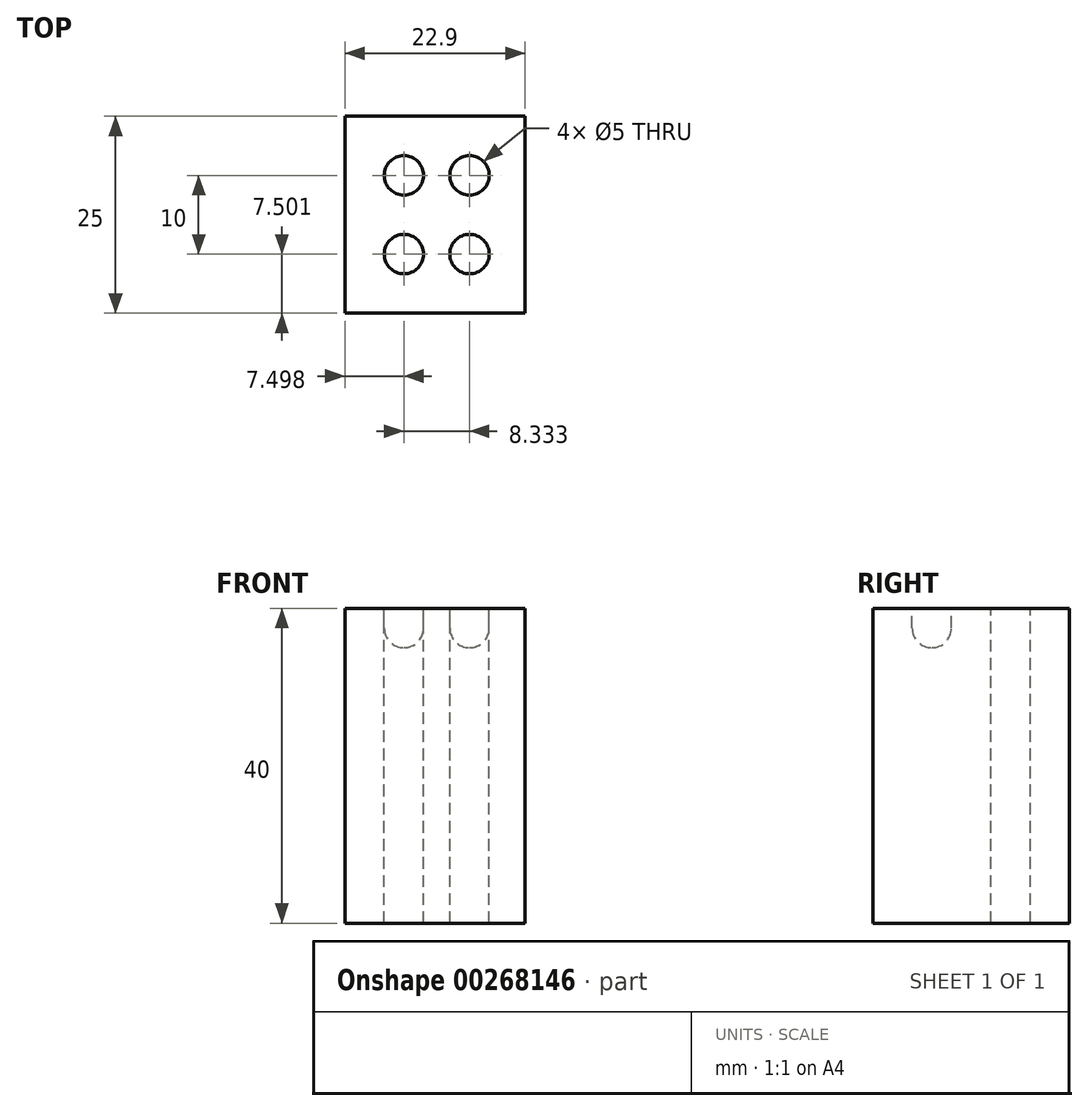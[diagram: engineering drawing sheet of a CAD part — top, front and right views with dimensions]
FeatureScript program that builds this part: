
annotation { "Feature Type Name" : "Feature", "Feature Type Description" : "" }
export const myFeature = defineFeature(function(context is Context, id is Id, definition is map)
    precondition{}
    {
        {
            var Q0;
            Q0=qCreatedBy(makeId("Top.planeOp"),FACE);
            var sketch = newSketch(context, id + "F0", { "sketchPlane" : qUnion([Q0])});
            skLineSegment(sketch, "E0.bottom", {"start": v(-42.9, 15.92) * mm, "end": v(-20, 15.92) * mm});
            skLineSegment(sketch, "E0.top", {"start": v(-42.9, -9.08) * mm, "end": v(-20, -9.08) * mm});
            skLineSegment(sketch, "E0.left", {"start": v(-42.9, 15.92) * mm, "end": v(-42.9, -9.08) * mm});
            skLineSegment(sketch, "E0.right", {"start": v(-20, 15.92) * mm, "end": v(-20, -9.08) * mm});
            skCircle(sketch, "E1", {"center": v(-35.4, 8.42) * mm, "radius": 2.5 * mm});
            skCircle(sketch, "E2.1.0.0", {"center": v(-27.06, 8.42) * mm, "radius": 2.5 * mm});
            skLineSegment(sketch, "E2.direction1", {"start": v(-35.4, 8.42) * mm, "end": v(-27.06, 8.42) * mm, "construction": true});
            skCircle(sketch, "E3", {"center": v(-35.4, -1.58) * mm, "radius": 2.5 * mm});
            skCircle(sketch, "E4.1.0.0", {"center": v(-27.06, -1.58) * mm, "radius": 2.5 * mm});
            skLineSegment(sketch, "E4.direction1", {"start": v(-35.4, -1.58) * mm, "end": v(-27.06, -1.58) * mm, "construction": true});
            skSolve(sketch);
        }
        {
            var Q0;
            Q0=makeQuery(id+"F0.imprint","IMPRINT",FACE,{"disambiguationData":[TD([[makeQuery(id+"F0.imprint","IMPRINT",EDGE,{"derivedFrom":sQuery(id+"F0.wireOp",EDGE,"E0.bottom")}),-1.0]])]});
            var Q1;
            Q1=makeQuery(id+"F0.imprint","IMPRINT",FACE,{"disambiguationData":[TD([[makeQuery(id+"F0.imprint","IMPRINT",EDGE,{"derivedFrom":sQuery(id+"F0.wireOp",EDGE,"E1")}),1.0]])]});
            var Q2;
            Q2=makeQuery(id+"F0.imprint","IMPRINT",FACE,{"disambiguationData":[TD([[makeQuery(id+"F0.imprint","IMPRINT",EDGE,{"derivedFrom":sQuery(id+"F0.wireOp",EDGE,"E2.1.0.0")}),1.0]])]});
            var Q3;
            Q3=makeQuery(id+"F0.imprint","IMPRINT",FACE,{"disambiguationData":[TD([[makeQuery(id+"F0.imprint","IMPRINT",EDGE,{"derivedFrom":sQuery(id+"F0.wireOp",EDGE,"E2.2.0.0")}),1.0]])]});
            var Q4;
            Q4=makeQuery(id+"F0.imprint","IMPRINT",FACE,{"disambiguationData":[TD([[makeQuery(id+"F0.imprint","IMPRINT",EDGE,{"derivedFrom":sQuery(id+"F0.wireOp",EDGE,"E2.3.0.0")}),1.0]])]});
            var Q5;
            Q5=makeQuery(id+"F0.imprint","IMPRINT",FACE,{"disambiguationData":[TD([[makeQuery(id+"F0.imprint","IMPRINT",EDGE,{"derivedFrom":sQuery(id+"F0.wireOp",EDGE,"E2.4.0.0")}),1.0]])]});
            var Q6;
            Q6=makeQuery(id+"F0.imprint","IMPRINT",FACE,{"disambiguationData":[TD([[makeQuery(id+"F0.imprint","IMPRINT",EDGE,{"derivedFrom":sQuery(id+"F0.wireOp",EDGE,"E2.5.0.0")}),1.0]])]});
            var Q7;
            Q7=makeQuery(id+"F0.imprint","IMPRINT",FACE,{"disambiguationData":[TD([[makeQuery(id+"F0.imprint","IMPRINT",EDGE,{"derivedFrom":sQuery(id+"F0.wireOp",EDGE,"E2.6.0.0")}),1.0]])]});
            var Q8;
            Q8=makeQuery(id+"F0.imprint","IMPRINT",FACE,{"disambiguationData":[TD([[makeQuery(id+"F0.imprint","IMPRINT",EDGE,{"derivedFrom":sQuery(id+"F0.wireOp",EDGE,"E2.7.0.0")}),1.0]])]});
            var Q9;
            Q9=makeQuery(id+"F0.imprint","IMPRINT",FACE,{"disambiguationData":[TD([[makeQuery(id+"F0.imprint","IMPRINT",EDGE,{"derivedFrom":sQuery(id+"F0.wireOp",EDGE,"E2.8.0.0")}),1.0]])]});
            var Q10;
            Q10=makeQuery(id+"F0.imprint","IMPRINT",FACE,{"disambiguationData":[TD([[makeQuery(id+"F0.imprint","IMPRINT",EDGE,{"derivedFrom":sQuery(id+"F0.wireOp",EDGE,"E2.9.0.0")}),1.0]])]});
            var Q11;
            Q11=makeQuery(id+"F0.imprint","IMPRINT",FACE,{"disambiguationData":[TD([[makeQuery(id+"F0.imprint","IMPRINT",EDGE,{"derivedFrom":sQuery(id+"F0.wireOp",EDGE,"E2.10.0.0")}),1.0]])]});
            var Q12;
            Q12=makeQuery(id+"F0.imprint","IMPRINT",FACE,{"disambiguationData":[TD([[makeQuery(id+"F0.imprint","IMPRINT",EDGE,{"derivedFrom":sQuery(id+"F0.wireOp",EDGE,"E2.11.0.0")}),1.0]])]});
            var Q13;
            Q13=makeQuery(id+"F0.imprint","IMPRINT",FACE,{"disambiguationData":[TD([[makeQuery(id+"F0.imprint","IMPRINT",EDGE,{"derivedFrom":sQuery(id+"F0.wireOp",EDGE,"E2.12.0.0")}),1.0]])]});
            var Q14;
            Q14=makeQuery(id+"F0.imprint","IMPRINT",FACE,{"disambiguationData":[TD([[makeQuery(id+"F0.imprint","IMPRINT",EDGE,{"derivedFrom":sQuery(id+"F0.wireOp",EDGE,"E2.13.0.0")}),1.0]])]});
            var Q15;
            Q15=makeQuery(id+"F0.imprint","IMPRINT",FACE,{"disambiguationData":[TD([[makeQuery(id+"F0.imprint","IMPRINT",EDGE,{"derivedFrom":sQuery(id+"F0.wireOp",EDGE,"E2.14.0.0")}),1.0]])]});
            var Q16;
            Q16=makeQuery(id+"F0.imprint","IMPRINT",FACE,{"disambiguationData":[TD([[makeQuery(id+"F0.imprint","IMPRINT",EDGE,{"derivedFrom":sQuery(id+"F0.wireOp",EDGE,"E4.14.0.0")}),1.0]])]});
            var Q17;
            Q17=makeQuery(id+"F0.imprint","IMPRINT",FACE,{"disambiguationData":[TD([[makeQuery(id+"F0.imprint","IMPRINT",EDGE,{"derivedFrom":sQuery(id+"F0.wireOp",EDGE,"E4.13.0.0")}),1.0]])]});
            var Q18;
            Q18=makeQuery(id+"F0.imprint","IMPRINT",FACE,{"disambiguationData":[TD([[makeQuery(id+"F0.imprint","IMPRINT",EDGE,{"derivedFrom":sQuery(id+"F0.wireOp",EDGE,"E4.12.0.0")}),1.0]])]});
            var Q19;
            Q19=makeQuery(id+"F0.imprint","IMPRINT",FACE,{"disambiguationData":[TD([[makeQuery(id+"F0.imprint","IMPRINT",EDGE,{"derivedFrom":sQuery(id+"F0.wireOp",EDGE,"E4.11.0.0")}),1.0]])]});
            var Q20;
            Q20=makeQuery(id+"F0.imprint","IMPRINT",FACE,{"disambiguationData":[TD([[makeQuery(id+"F0.imprint","IMPRINT",EDGE,{"derivedFrom":sQuery(id+"F0.wireOp",EDGE,"E4.10.0.0")}),1.0]])]});
            var Q21;
            Q21=makeQuery(id+"F0.imprint","IMPRINT",FACE,{"disambiguationData":[TD([[makeQuery(id+"F0.imprint","IMPRINT",EDGE,{"derivedFrom":sQuery(id+"F0.wireOp",EDGE,"E4.9.0.0")}),1.0]])]});
            var Q22;
            Q22=makeQuery(id+"F0.imprint","IMPRINT",FACE,{"disambiguationData":[TD([[makeQuery(id+"F0.imprint","IMPRINT",EDGE,{"derivedFrom":sQuery(id+"F0.wireOp",EDGE,"E4.8.0.0")}),1.0]])]});
            var Q23;
            Q23=makeQuery(id+"F0.imprint","IMPRINT",FACE,{"disambiguationData":[TD([[makeQuery(id+"F0.imprint","IMPRINT",EDGE,{"derivedFrom":sQuery(id+"F0.wireOp",EDGE,"E4.7.0.0")}),1.0]])]});
            var Q24;
            Q24=makeQuery(id+"F0.imprint","IMPRINT",FACE,{"disambiguationData":[TD([[makeQuery(id+"F0.imprint","IMPRINT",EDGE,{"derivedFrom":sQuery(id+"F0.wireOp",EDGE,"E4.6.0.0")}),1.0]])]});
            var Q25;
            Q25=makeQuery(id+"F0.imprint","IMPRINT",FACE,{"disambiguationData":[TD([[makeQuery(id+"F0.imprint","IMPRINT",EDGE,{"derivedFrom":sQuery(id+"F0.wireOp",EDGE,"E4.5.0.0")}),1.0]])]});
            var Q26;
            Q26=makeQuery(id+"F0.imprint","IMPRINT",FACE,{"disambiguationData":[TD([[makeQuery(id+"F0.imprint","IMPRINT",EDGE,{"derivedFrom":sQuery(id+"F0.wireOp",EDGE,"E4.4.0.0")}),1.0]])]});
            var Q27;
            Q27=makeQuery(id+"F0.imprint","IMPRINT",FACE,{"disambiguationData":[TD([[makeQuery(id+"F0.imprint","IMPRINT",EDGE,{"derivedFrom":sQuery(id+"F0.wireOp",EDGE,"E4.3.0.0")}),1.0]])]});
            var Q28;
            Q28=makeQuery(id+"F0.imprint","IMPRINT",FACE,{"disambiguationData":[TD([[makeQuery(id+"F0.imprint","IMPRINT",EDGE,{"derivedFrom":sQuery(id+"F0.wireOp",EDGE,"E4.2.0.0")}),1.0]])]});
            var Q29;
            Q29=makeQuery(id+"F0.imprint","IMPRINT",FACE,{"disambiguationData":[TD([[makeQuery(id+"F0.imprint","IMPRINT",EDGE,{"derivedFrom":sQuery(id+"F0.wireOp",EDGE,"E4.1.0.0")}),1.0]])]});
            var Q30;
            Q30=makeQuery(id+"F0.imprint","IMPRINT",FACE,{"disambiguationData":[TD([[makeQuery(id+"F0.imprint","IMPRINT",EDGE,{"derivedFrom":sQuery(id+"F0.wireOp",EDGE,"E3")}),1.0]])]});
            extrude(context, id + "F1", {"entities" : qUnion([Q0, Q1, Q2, Q3, Q4, Q5, Q6, Q7, Q8, Q9, Q10, Q11, Q12, Q13, Q14, Q15, Q16, Q17, Q18, Q19, Q20, Q21, Q22, Q23, Q24, Q25, Q26, Q27, Q28, Q29, Q30]), "oppositeDirection" : true, "depth" : 40 * mm});
        }
        {
            var Q0;
            Q0=makeQuery(id+"F0.imprint","IMPRINT",FACE,{"disambiguationData":[TD([[makeQuery(id+"F0.imprint","IMPRINT",EDGE,{"derivedFrom":sQuery(id+"F0.wireOp",EDGE,"E1")}),1.0]])]});
            var Q1;
            Q1=makeQuery(id+"F0.imprint","IMPRINT",FACE,{"disambiguationData":[TD([[makeQuery(id+"F0.imprint","IMPRINT",EDGE,{"derivedFrom":sQuery(id+"F0.wireOp",EDGE,"E2.1.0.0")}),1.0]])]});
            var Q2;
            Q2=makeQuery(id+"F0.imprint","IMPRINT",FACE,{"disambiguationData":[TD([[makeQuery(id+"F0.imprint","IMPRINT",EDGE,{"derivedFrom":sQuery(id+"F0.wireOp",EDGE,"E2.2.0.0")}),1.0]])]});
            var Q3;
            Q3=makeQuery(id+"F0.imprint","IMPRINT",FACE,{"disambiguationData":[TD([[makeQuery(id+"F0.imprint","IMPRINT",EDGE,{"derivedFrom":sQuery(id+"F0.wireOp",EDGE,"E2.3.0.0")}),1.0]])]});
            var Q4;
            Q4=makeQuery(id+"F0.imprint","IMPRINT",FACE,{"disambiguationData":[TD([[makeQuery(id+"F0.imprint","IMPRINT",EDGE,{"derivedFrom":sQuery(id+"F0.wireOp",EDGE,"E2.4.0.0")}),1.0]])]});
            var Q5;
            Q5=makeQuery(id+"F0.imprint","IMPRINT",FACE,{"disambiguationData":[TD([[makeQuery(id+"F0.imprint","IMPRINT",EDGE,{"derivedFrom":sQuery(id+"F0.wireOp",EDGE,"E2.5.0.0")}),1.0]])]});
            var Q6;
            Q6=makeQuery(id+"F0.imprint","IMPRINT",FACE,{"disambiguationData":[TD([[makeQuery(id+"F0.imprint","IMPRINT",EDGE,{"derivedFrom":sQuery(id+"F0.wireOp",EDGE,"E2.6.0.0")}),1.0]])]});
            var Q7;
            Q7=makeQuery(id+"F0.imprint","IMPRINT",FACE,{"disambiguationData":[TD([[makeQuery(id+"F0.imprint","IMPRINT",EDGE,{"derivedFrom":sQuery(id+"F0.wireOp",EDGE,"E2.7.0.0")}),1.0]])]});
            var Q8;
            Q8=makeQuery(id+"F0.imprint","IMPRINT",FACE,{"disambiguationData":[TD([[makeQuery(id+"F0.imprint","IMPRINT",EDGE,{"derivedFrom":sQuery(id+"F0.wireOp",EDGE,"E2.8.0.0")}),1.0]])]});
            var Q9;
            Q9=makeQuery(id+"F0.imprint","IMPRINT",FACE,{"disambiguationData":[TD([[makeQuery(id+"F0.imprint","IMPRINT",EDGE,{"derivedFrom":sQuery(id+"F0.wireOp",EDGE,"E2.9.0.0")}),1.0]])]});
            var Q10;
            Q10=makeQuery(id+"F0.imprint","IMPRINT",FACE,{"disambiguationData":[TD([[makeQuery(id+"F0.imprint","IMPRINT",EDGE,{"derivedFrom":sQuery(id+"F0.wireOp",EDGE,"E2.10.0.0")}),1.0]])]});
            var Q11;
            Q11=makeQuery(id+"F0.imprint","IMPRINT",FACE,{"disambiguationData":[TD([[makeQuery(id+"F0.imprint","IMPRINT",EDGE,{"derivedFrom":sQuery(id+"F0.wireOp",EDGE,"E2.11.0.0")}),1.0]])]});
            var Q12;
            Q12=makeQuery(id+"F0.imprint","IMPRINT",FACE,{"disambiguationData":[TD([[makeQuery(id+"F0.imprint","IMPRINT",EDGE,{"derivedFrom":sQuery(id+"F0.wireOp",EDGE,"E2.12.0.0")}),1.0]])]});
            var Q13;
            Q13=makeQuery(id+"F0.imprint","IMPRINT",FACE,{"disambiguationData":[TD([[makeQuery(id+"F0.imprint","IMPRINT",EDGE,{"derivedFrom":sQuery(id+"F0.wireOp",EDGE,"E2.13.0.0")}),1.0]])]});
            var Q14;
            Q14=makeQuery(id+"F0.imprint","IMPRINT",FACE,{"disambiguationData":[TD([[makeQuery(id+"F0.imprint","IMPRINT",EDGE,{"derivedFrom":sQuery(id+"F0.wireOp",EDGE,"E2.14.0.0")}),1.0]])]});
            extrude(context, id + "F2", {"entities" : qUnion([Q0, Q1, Q2, Q3, Q4, Q5, Q6, Q7, Q8, Q9, Q10, Q11, Q12, Q13, Q14]), "operationType" : NewBodyOperationType.REMOVE, "oppositeDirection" : true, "depth" : 40 * mm});
        }
        {
            var Q0;
            Q0=makeQuery(id+"F0.imprint","IMPRINT",FACE,{"disambiguationData":[TD([[makeQuery(id+"F0.imprint","IMPRINT",EDGE,{"derivedFrom":sQuery(id+"F0.wireOp",EDGE,"E3")}),1.0]])]});
            var Q1;
            Q1=makeQuery(id+"F0.imprint","IMPRINT",FACE,{"disambiguationData":[TD([[makeQuery(id+"F0.imprint","IMPRINT",EDGE,{"derivedFrom":sQuery(id+"F0.wireOp",EDGE,"E4.1.0.0")}),1.0]])]});
            var Q2;
            Q2=makeQuery(id+"F0.imprint","IMPRINT",FACE,{"disambiguationData":[TD([[makeQuery(id+"F0.imprint","IMPRINT",EDGE,{"derivedFrom":sQuery(id+"F0.wireOp",EDGE,"E4.2.0.0")}),1.0]])]});
            var Q3;
            Q3=makeQuery(id+"F0.imprint","IMPRINT",FACE,{"disambiguationData":[TD([[makeQuery(id+"F0.imprint","IMPRINT",EDGE,{"derivedFrom":sQuery(id+"F0.wireOp",EDGE,"E4.3.0.0")}),1.0]])]});
            var Q4;
            Q4=makeQuery(id+"F0.imprint","IMPRINT",FACE,{"disambiguationData":[TD([[makeQuery(id+"F0.imprint","IMPRINT",EDGE,{"derivedFrom":sQuery(id+"F0.wireOp",EDGE,"E4.4.0.0")}),1.0]])]});
            var Q5;
            Q5=makeQuery(id+"F0.imprint","IMPRINT",FACE,{"disambiguationData":[TD([[makeQuery(id+"F0.imprint","IMPRINT",EDGE,{"derivedFrom":sQuery(id+"F0.wireOp",EDGE,"E4.5.0.0")}),1.0]])]});
            var Q6;
            Q6=makeQuery(id+"F0.imprint","IMPRINT",FACE,{"disambiguationData":[TD([[makeQuery(id+"F0.imprint","IMPRINT",EDGE,{"derivedFrom":sQuery(id+"F0.wireOp",EDGE,"E4.6.0.0")}),1.0]])]});
            var Q7;
            Q7=makeQuery(id+"F0.imprint","IMPRINT",FACE,{"disambiguationData":[TD([[makeQuery(id+"F0.imprint","IMPRINT",EDGE,{"derivedFrom":sQuery(id+"F0.wireOp",EDGE,"E4.7.0.0")}),1.0]])]});
            var Q8;
            Q8=makeQuery(id+"F0.imprint","IMPRINT",FACE,{"disambiguationData":[TD([[makeQuery(id+"F0.imprint","IMPRINT",EDGE,{"derivedFrom":sQuery(id+"F0.wireOp",EDGE,"E4.8.0.0")}),1.0]])]});
            var Q9;
            Q9=makeQuery(id+"F0.imprint","IMPRINT",FACE,{"disambiguationData":[TD([[makeQuery(id+"F0.imprint","IMPRINT",EDGE,{"derivedFrom":sQuery(id+"F0.wireOp",EDGE,"E4.9.0.0")}),1.0]])]});
            var Q10;
            Q10=makeQuery(id+"F0.imprint","IMPRINT",FACE,{"disambiguationData":[TD([[makeQuery(id+"F0.imprint","IMPRINT",EDGE,{"derivedFrom":sQuery(id+"F0.wireOp",EDGE,"E4.10.0.0")}),1.0]])]});
            var Q11;
            Q11=makeQuery(id+"F0.imprint","IMPRINT",FACE,{"disambiguationData":[TD([[makeQuery(id+"F0.imprint","IMPRINT",EDGE,{"derivedFrom":sQuery(id+"F0.wireOp",EDGE,"E4.11.0.0")}),1.0]])]});
            var Q12;
            Q12=makeQuery(id+"F0.imprint","IMPRINT",FACE,{"disambiguationData":[TD([[makeQuery(id+"F0.imprint","IMPRINT",EDGE,{"derivedFrom":sQuery(id+"F0.wireOp",EDGE,"E4.12.0.0")}),1.0]])]});
            var Q13;
            Q13=makeQuery(id+"F0.imprint","IMPRINT",FACE,{"disambiguationData":[TD([[makeQuery(id+"F0.imprint","IMPRINT",EDGE,{"derivedFrom":sQuery(id+"F0.wireOp",EDGE,"E4.13.0.0")}),1.0]])]});
            var Q14;
            Q14=makeQuery(id+"F0.imprint","IMPRINT",FACE,{"disambiguationData":[TD([[makeQuery(id+"F0.imprint","IMPRINT",EDGE,{"derivedFrom":sQuery(id+"F0.wireOp",EDGE,"E4.14.0.0")}),1.0]])]});
            extrude(context, id + "F3", {"entities" : qUnion([Q0, Q1, Q2, Q3, Q4, Q5, Q6, Q7, Q8, Q9, Q10, Q11, Q12, Q13, Q14]), "operationType" : NewBodyOperationType.REMOVE, "oppositeDirection" : true, "depth" : 5 * mm});
        }
        {
            var Q0;
            Q0=makeQuery(id+"F3.boolean.opBoolean","COPY",EDGE,{"derivedFrom":makeQuery(id+"F3.opExtrude","CAP_EDGE",EDGE,{"disambiguationData":[OSD([sQuery(id+"F0.wireOp",EDGE,"E3")])],"isStart":false})});
            var Q1;
            Q1=makeQuery(id+"F3.boolean.opBoolean","COPY",EDGE,{"derivedFrom":makeQuery(id+"F3.opExtrude","CAP_EDGE",EDGE,{"disambiguationData":[OSD([sQuery(id+"F0.wireOp",EDGE,"E4.1.0.0")])],"isStart":false})});
            var Q2;
            Q2=makeQuery(id+"F3.boolean.opBoolean","COPY",EDGE,{"derivedFrom":makeQuery(id+"F3.opExtrude","CAP_EDGE",EDGE,{"disambiguationData":[OSD([sQuery(id+"F0.wireOp",EDGE,"E4.2.0.0")])],"isStart":false})});
            var Q3;
            Q3=makeQuery(id+"F3.boolean.opBoolean","COPY",EDGE,{"derivedFrom":makeQuery(id+"F3.opExtrude","CAP_EDGE",EDGE,{"disambiguationData":[OSD([sQuery(id+"F0.wireOp",EDGE,"E4.3.0.0")])],"isStart":false})});
            var Q4;
            Q4=makeQuery(id+"F3.boolean.opBoolean","COPY",EDGE,{"derivedFrom":makeQuery(id+"F3.opExtrude","CAP_EDGE",EDGE,{"disambiguationData":[OSD([sQuery(id+"F0.wireOp",EDGE,"E4.4.0.0")])],"isStart":false})});
            var Q5;
            Q5=makeQuery(id+"F3.boolean.opBoolean","COPY",EDGE,{"derivedFrom":makeQuery(id+"F3.opExtrude","CAP_EDGE",EDGE,{"disambiguationData":[OSD([sQuery(id+"F0.wireOp",EDGE,"E4.5.0.0")])],"isStart":false})});
            var Q6;
            Q6=makeQuery(id+"F3.boolean.opBoolean","COPY",EDGE,{"derivedFrom":makeQuery(id+"F3.opExtrude","CAP_EDGE",EDGE,{"disambiguationData":[OSD([sQuery(id+"F0.wireOp",EDGE,"E4.6.0.0")])],"isStart":false})});
            var Q7;
            Q7=makeQuery(id+"F3.boolean.opBoolean","COPY",EDGE,{"derivedFrom":makeQuery(id+"F3.opExtrude","CAP_EDGE",EDGE,{"disambiguationData":[OSD([sQuery(id+"F0.wireOp",EDGE,"E4.7.0.0")])],"isStart":false})});
            var Q8;
            Q8=makeQuery(id+"F3.boolean.opBoolean","COPY",FACE,{"derivedFrom":makeQuery(id+"F3.opExtrude","CAP_FACE",FACE,{"disambiguationData":[OSD([sQuery(id+"F0.wireOp",EDGE,"E4.8.0.0")])],"isStart":false})});
            var Q9;
            Q9=makeQuery(id+"F3.boolean.opBoolean","COPY",EDGE,{"derivedFrom":makeQuery(id+"F3.opExtrude","CAP_EDGE",EDGE,{"disambiguationData":[OSD([sQuery(id+"F0.wireOp",EDGE,"E4.9.0.0")])],"isStart":false})});
            var Q10;
            Q10=makeQuery(id+"F3.boolean.opBoolean","COPY",EDGE,{"derivedFrom":makeQuery(id+"F3.opExtrude","CAP_EDGE",EDGE,{"disambiguationData":[OSD([sQuery(id+"F0.wireOp",EDGE,"E4.10.0.0")])],"isStart":false})});
            var Q11;
            Q11=makeQuery(id+"F3.boolean.opBoolean","COPY",FACE,{"derivedFrom":makeQuery(id+"F3.opExtrude","CAP_FACE",FACE,{"disambiguationData":[OSD([sQuery(id+"F0.wireOp",EDGE,"E4.11.0.0")])],"isStart":false})});
            var Q12;
            Q12=makeQuery(id+"F3.boolean.opBoolean","COPY",FACE,{"derivedFrom":makeQuery(id+"F3.opExtrude","CAP_FACE",FACE,{"disambiguationData":[OSD([sQuery(id+"F0.wireOp",EDGE,"E4.12.0.0")])],"isStart":false})});
            var Q13;
            Q13=makeQuery(id+"F3.boolean.opBoolean","COPY",EDGE,{"derivedFrom":makeQuery(id+"F3.opExtrude","CAP_EDGE",EDGE,{"disambiguationData":[OSD([sQuery(id+"F0.wireOp",EDGE,"E4.13.0.0")])],"isStart":false})});
            var Q14;
            Q14=makeQuery(id+"F3.boolean.opBoolean","COPY",EDGE,{"derivedFrom":makeQuery(id+"F3.opExtrude","CAP_EDGE",EDGE,{"disambiguationData":[OSD([sQuery(id+"F0.wireOp",EDGE,"E4.14.0.0")])],"isStart":false})});
            fillet(context, id + "F4", {"entities" : qUnion([Q0, Q1, Q2, Q3, Q4, Q5, Q6, Q7, Q8, Q9, Q10, Q11, Q12, Q13, Q14]), "radius" : 2.5 * mm, "tangentPropagation" : true, "allowEdgeOverflow" : false});
        }
    });
